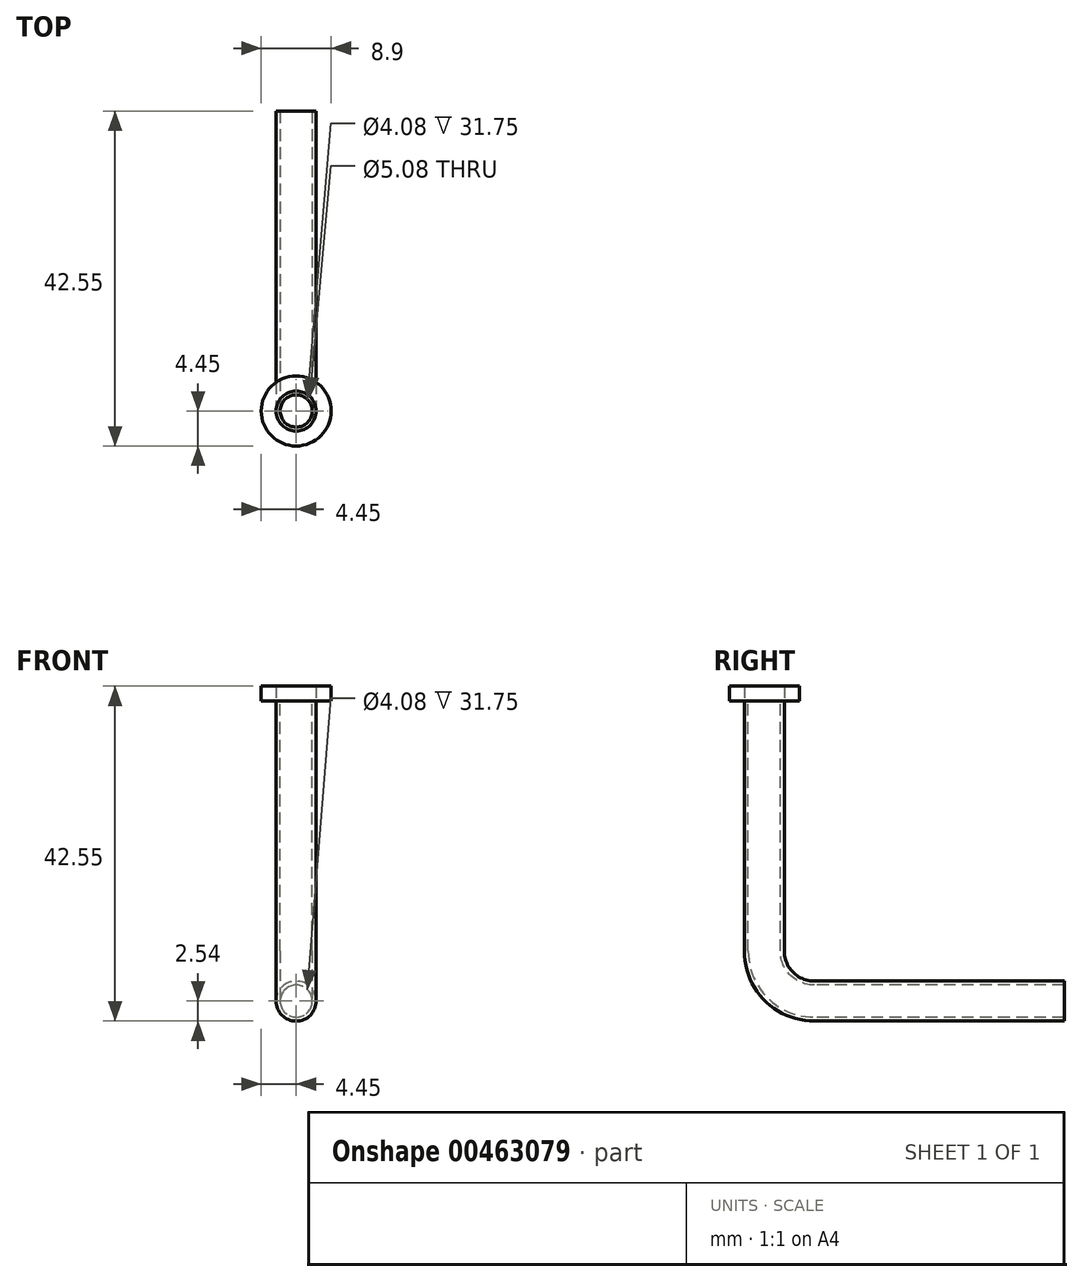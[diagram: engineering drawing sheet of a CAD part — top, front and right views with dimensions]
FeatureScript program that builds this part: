
annotation { "Feature Type Name" : "Feature", "Feature Type Description" : "" }
export const myFeature = defineFeature(function(context is Context, id is Id, definition is map)
    precondition{}
    {
        {
            var Q0;
            Q0=qCreatedBy(makeId("Front.planeOp"),FACE);
            var sketch = newSketch(context, id + "F0", { "sketchPlane" : qUnion([Q0])});
            skCircle(sketch, "E0", {"center": v(0, 0) * mm, "radius": 2.54 * mm});
            skSolve(sketch);
        }
        {
            var Q0;
            Q0=qCreatedBy(makeId("Right.planeOp"),FACE);
            var sketch = newSketch(context, id + "F1", { "sketchPlane" : qUnion([Q0])});
            skLineSegment(sketch, "E1", {"start": v(0, 0) * mm, "end": v(-31.75, 0) * mm});
            skLineSegment(sketch, "E2", {"start": v(-38.1, 6.35) * mm, "end": v(-38.1, 38.1) * mm});
            skPoint(sketch, "E3.visualSharp", {"position": v(-38.1, 0) * mm});
            skArc(sketch, "E3.filletArc", {"start": v(-38.1, 6.35) * mm, "mid": v(-36.24, 1.86) * mm, "end": v(-31.75, 0) * mm});
            skSolve(sketch);
        }
        {
            var Q0;
            Q0=makeQuery(id+"F0.imprint","IMPRINT",FACE,{"disambiguationData":[TD([[makeQuery(id+"F0.imprint","IMPRINT",EDGE,{"derivedFrom":sQuery(id+"F0.wireOp",EDGE,"E0")}),1.0]])]});
            var Q1;
            Q1=sQuery(id+"F1.wireOp",EDGE,"E1");
            var Q2;
            Q2=sQuery(id+"F1.wireOp",EDGE,"E3.filletArc");
            var Q3;
            Q3=sQuery(id+"F1.wireOp",EDGE,"E2");
            sweep(context, id + "F2", {"profiles" : qUnion([Q0]), "path" : qUnion([Q1, Q2, Q3])});
        }
        {
            var Q0;
            Q0=makeQuery(id+"F2.opSweep","CAP_FACE",FACE,{"disambiguationData":[OSD([sQuery(id+"F0.wireOp",EDGE,"E0"),sQuery(id+"F1.wireOp",VERTEX,"E2.end")])],"isStart":false});
            var sketch = newSketch(context, id + "F3", { "sketchPlane" : qUnion([Q0])});
            skCircle(sketch, "E4", {"center": v(0, -38.1) * mm, "radius": 4.45 * mm});
            skSolve(sketch);
        }
        {
            var Q0;
            Q0=makeQuery(id+"F3.imprint","IMPRINT",FACE,{"disambiguationData":[TD([[makeQuery(id+"F3.imprint","IMPRINT",EDGE,{"derivedFrom":sQuery(id+"F3.wireOp",EDGE,"E4")}),1.0]])]});
            extrude(context, id + "F4", {"entities" : qUnion([Q0]), "depth" : 1.9 * mm});
        }
        {
            var Q0;
            Q0=makeQuery(id+"F2.opSweep","CAP_FACE",FACE,{"disambiguationData":[OSD([sQuery(id+"F0.wireOp",EDGE,"E0"),sQuery(id+"F1.wireOp",VERTEX,"E1.start")])],"isStart":true});
            var sketch = newSketch(context, id + "F5", { "sketchPlane" : qUnion([Q0])});
            skCircle(sketch, "E5", {"center": v(0, 0) * mm, "radius": 2.04 * mm});
            skSolve(sketch);
        }
        {
            var Q0;
            Q0=makeQuery(id+"F5.imprint","IMPRINT",FACE,{"disambiguationData":[TD([[makeQuery(id+"F5.imprint","IMPRINT",EDGE,{"derivedFrom":sQuery(id+"F5.wireOp",EDGE,"E5")}),1.0]])]});
            var Q1;
            Q1=qConstructionFilter(qBodyType(qCreatedBy(id+"F1",EDGE),BodyType.WIRE),ConstructionObject.NO);
            sweep(context, id + "F6", {"operationType" : NewBodyOperationType.REMOVE, "profiles" : qUnion([Q0]), "path" : qUnion([Q1])});
        }
    });
